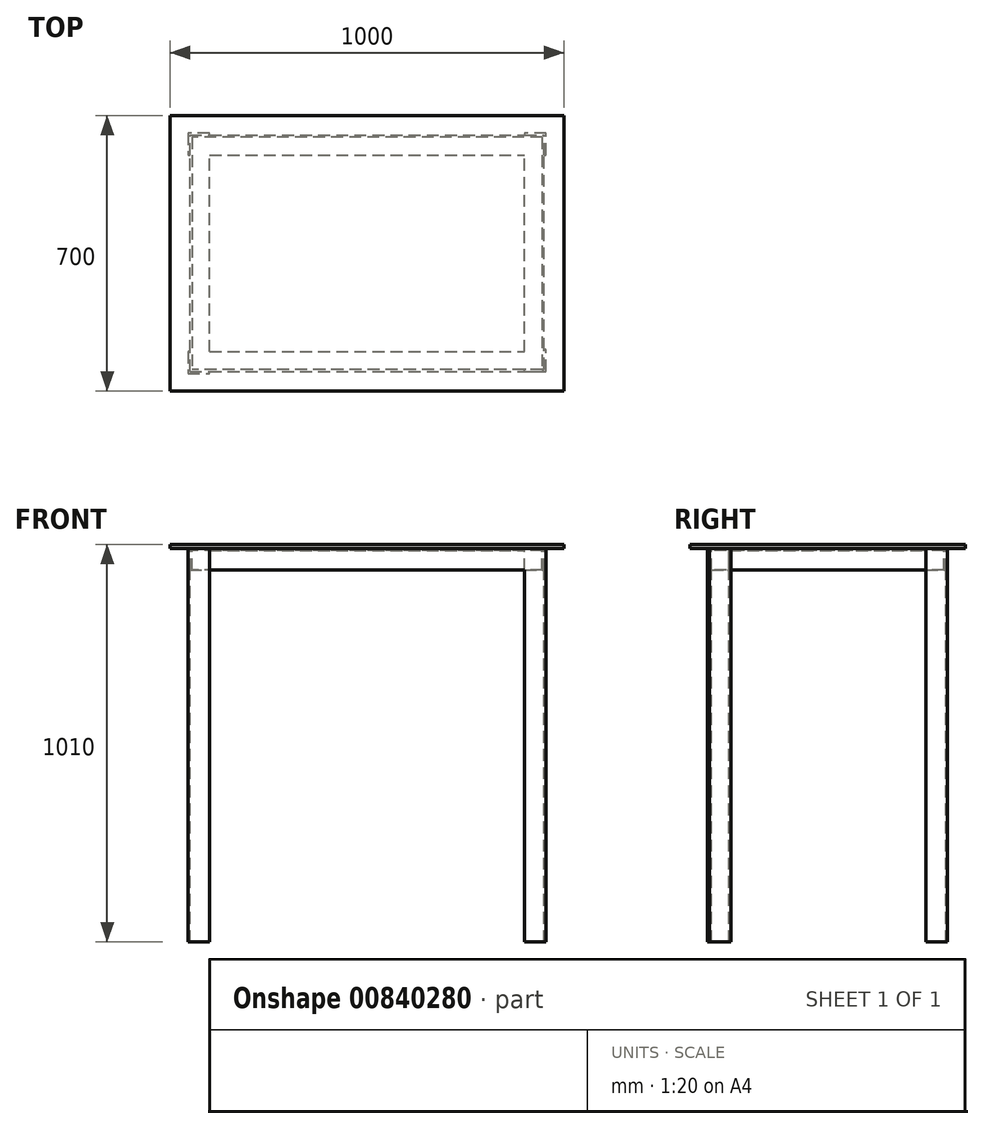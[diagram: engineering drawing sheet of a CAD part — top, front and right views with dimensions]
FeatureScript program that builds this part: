
annotation { "Feature Type Name" : "Feature", "Feature Type Description" : "" }
export const myFeature = defineFeature(function(context is Context, id is Id, definition is map)
    precondition{}
    {
        {
            var Q0;
            Q0=qCreatedBy(makeId("Top.planeOp"),FACE);
            var sketch = newSketch(context, id + "F0", { "sketchPlane" : qUnion([Q0])});
            skLineSegment(sketch, "E0.bottom", {"start": v(-59.03, 659.23) * mm, "end": v(940.97, 659.23) * mm});
            skLineSegment(sketch, "E0.top", {"start": v(-59.03, -40.77) * mm, "end": v(940.97, -40.77) * mm});
            skLineSegment(sketch, "E0.left", {"start": v(-59.03, 659.23) * mm, "end": v(-59.03, -40.77) * mm});
            skLineSegment(sketch, "E0.right", {"start": v(940.97, 659.23) * mm, "end": v(940.97, -40.77) * mm});
            skSolve(sketch);
        }
        {
            var Q0;
            Q0=makeQuery(id+"F0.imprint","IMPRINT",FACE,{"disambiguationData":[TD([[makeQuery(id+"F0.imprint","IMPRINT",EDGE,{"derivedFrom":sQuery(id+"F0.wireOp",EDGE,"E0.bottom")}),-1.0]])]});
            extrude(context, id + "F1", {"entities" : qUnion([Q0]), "oppositeDirection" : true, "depth" : 10 * mm, "offsetDistance" : 25 * mm});
        }
        {
            var Q0;
            Q0=makeQuery(id+"F1.opExtrude","CAP_FACE",FACE,{"disambiguationData":[OSD([sQuery(id+"F0.wireOp",EDGE,"E0.bottom"),sQuery(id+"F0.wireOp",EDGE,"E0.top"),sQuery(id+"F0.wireOp",EDGE,"E0.left"),sQuery(id+"F0.wireOp",EDGE,"E0.right")])],"isStart":false});
            var sketch = newSketch(context, id + "F2", { "sketchPlane" : qUnion([Q0])});
            skLineSegment(sketch, "E1.bottom", {"start": v(-9.03, -9.23) * mm, "end": v(890.97, -9.23) * mm});
            skLineSegment(sketch, "E1.top", {"start": v(-9.03, -609.23) * mm, "end": v(890.97, -609.23) * mm});
            skLineSegment(sketch, "E1.left", {"start": v(-9.03, -9.23) * mm, "end": v(-9.03, -609.23) * mm});
            skLineSegment(sketch, "E1.right", {"start": v(890.97, -9.23) * mm, "end": v(890.97, -609.23) * mm});
            skLineSegment(sketch, "E2.bottom", {"start": v(40.97, -59.23) * mm, "end": v(840.97, -59.23) * mm});
            skLineSegment(sketch, "E2.top", {"start": v(40.97, -559.23) * mm, "end": v(840.97, -559.23) * mm});
            skLineSegment(sketch, "E2.left", {"start": v(40.97, -59.23) * mm, "end": v(40.97, -559.23) * mm});
            skLineSegment(sketch, "E2.right", {"start": v(840.97, -59.23) * mm, "end": v(840.97, -559.23) * mm});
            skSolve(sketch);
        }
        {
            var Q0;
            Q0=makeQuery(id+"F2.imprint","IMPRINT",FACE,{"disambiguationData":[TD([[makeQuery(id+"F2.imprint","IMPRINT",EDGE,{"derivedFrom":sQuery(id+"F2.wireOp",EDGE,"E1.bottom")}),-1.0]])]});
            extrude(context, id + "F3", {"entities" : qUnion([Q0]), "operationType" : NewBodyOperationType.ADD, "oppositeDirection" : true, "depth" : -5 * mm, "offsetDistance" : 25 * mm});
        }
        {
            var Q0;
            Q0=makeQuery(id+"F3.opExtrude","CAP_FACE",FACE,{"disambiguationData":[OSD([sQuery(id+"F2.wireOp",EDGE,"E1.bottom"),sQuery(id+"F2.wireOp",EDGE,"E1.top"),sQuery(id+"F2.wireOp",EDGE,"E1.left"),sQuery(id+"F2.wireOp",EDGE,"E1.right"),sQuery(id+"F2.wireOp",EDGE,"E2.bottom"),sQuery(id+"F2.wireOp",EDGE,"E2.top"),sQuery(id+"F2.wireOp",EDGE,"E2.left"),sQuery(id+"F2.wireOp",EDGE,"E2.right")])],"isStart":false});
            var sketch = newSketch(context, id + "F4", { "sketchPlane" : qUnion([Q0])});
            skLineSegment(sketch, "E3.bottom", {"start": v(-9.03, -9.23) * mm, "end": v(890.97, -9.23) * mm});
            skLineSegment(sketch, "E3.top", {"start": v(-9.03, -609.23) * mm, "end": v(890.97, -609.23) * mm});
            skLineSegment(sketch, "E3.left", {"start": v(-9.03, -9.23) * mm, "end": v(-9.03, -609.23) * mm});
            skLineSegment(sketch, "E3.right", {"start": v(890.97, -9.23) * mm, "end": v(890.97, -609.23) * mm});
            skLineSegment(sketch, "E4.bottom", {"start": v(885.97, -604.23) * mm, "end": v(-4.03, -604.23) * mm});
            skLineSegment(sketch, "E4.top", {"start": v(885.97, -14.23) * mm, "end": v(-4.03, -14.23) * mm});
            skLineSegment(sketch, "E4.left", {"start": v(885.97, -604.23) * mm, "end": v(885.97, -14.23) * mm});
            skLineSegment(sketch, "E4.right", {"start": v(-4.03, -604.23) * mm, "end": v(-4.03, -14.23) * mm});
            skSolve(sketch);
        }
        {
            var Q0;
            Q0 = qSketchRegion(id + "F4", true);
            extrude(context, id + "F5", {"entities" : qUnion([Q0]), "operationType" : NewBodyOperationType.ADD, "depth" : 50 * mm, "offsetDistance" : 25 * mm});
        }
        {
            var Q0;
            {var subQ0=sQuery(id+"F0.wireOp",EDGE,"E0.left");var subQ1=sQuery(id+"F0.wireOp",EDGE,"E0.top");var subQ2=sQuery(id+"F0.wireOp",EDGE,"E0.right");var subQ3=sQuery(id+"F0.wireOp",EDGE,"E0.bottom");Q0=makeQuery(id+"F3.boolean.opBoolean","SPLIT",FACE,{"disambiguationData":[TD([makeQuery(id+"F1.opExtrude","SWEPT_FACE",FACE,{"disambiguationData":[OSD([subQ3])]})])],"derivedFrom":makeQuery(id+"F1.opExtrude","CAP_FACE",FACE,{"disambiguationData":[OSD([subQ3,subQ1,subQ0,subQ2])],"isStart":false})});}
            var sketch = newSketch(context, id + "F6", { "sketchPlane" : qUnion([Q0])});
            skLineSegment(sketch, "E5", {"start": v(-9.03, -9.23) * mm, "end": v(-9.03, -59.23) * mm});
            skLineSegment(sketch, "E6", {"start": v(-9.03, -59.23) * mm, "end": v(-14.03, -59.23) * mm});
            skLineSegment(sketch, "E7", {"start": v(-14.03, -59.23) * mm, "end": v(-14.03, -4.23) * mm});
            skLineSegment(sketch, "E8", {"start": v(-14.03, -4.23) * mm, "end": v(40.97, -4.23) * mm});
            skLineSegment(sketch, "E9", {"start": v(40.97, -4.23) * mm, "end": v(40.97, -9.23) * mm});
            skLineSegment(sketch, "E10", {"start": v(40.97, -9.23) * mm, "end": v(-9.03, -9.23) * mm});
            skLineSegment(sketch, "E11", {"start": v(-9.03, -609.23) * mm, "end": v(40.97, -609.23) * mm});
            skLineSegment(sketch, "E12", {"start": v(40.97, -609.23) * mm, "end": v(40.97, -614.23) * mm});
            skLineSegment(sketch, "E13", {"start": v(40.97, -614.23) * mm, "end": v(-14.03, -614.23) * mm});
            skLineSegment(sketch, "E14", {"start": v(-14.03, -614.23) * mm, "end": v(-14.03, -559.23) * mm});
            skLineSegment(sketch, "E15", {"start": v(-14.03, -559.23) * mm, "end": v(-9.03, -559.23) * mm});
            skLineSegment(sketch, "E16", {"start": v(-9.03, -559.23) * mm, "end": v(-9.03, -609.23) * mm});
            skLineSegment(sketch, "E17", {"start": v(890.97, -14.23) * mm, "end": v(840.97, -14.23) * mm});
            skLineSegment(sketch, "E18", {"start": v(840.97, -14.23) * mm, "end": v(840.97, -9.23) * mm});
            skLineSegment(sketch, "E19", {"start": v(840.97, -9.23) * mm, "end": v(895.97, -9.23) * mm});
            skLineSegment(sketch, "E20", {"start": v(895.97, -9.23) * mm, "end": v(895.97, -64.23) * mm});
            skLineSegment(sketch, "E21", {"start": v(895.97, -64.23) * mm, "end": v(890.97, -64.23) * mm});
            skLineSegment(sketch, "E22", {"start": v(890.97, -64.23) * mm, "end": v(890.97, -14.23) * mm});
            skLineSegment(sketch, "E23", {"start": v(890.97, -609.23) * mm, "end": v(890.97, -559.23) * mm});
            skLineSegment(sketch, "E24", {"start": v(890.97, -559.23) * mm, "end": v(895.97, -559.23) * mm});
            skLineSegment(sketch, "E25", {"start": v(895.97, -559.23) * mm, "end": v(895.97, -614.23) * mm});
            skLineSegment(sketch, "E26", {"start": v(895.97, -614.23) * mm, "end": v(840.97, -614.23) * mm});
            skLineSegment(sketch, "E27", {"start": v(840.97, -614.23) * mm, "end": v(840.97, -609.23) * mm});
            skLineSegment(sketch, "E28", {"start": v(840.97, -609.23) * mm, "end": v(890.97, -609.23) * mm});
            skSolve(sketch);
        }
        {
            var Q0;
            Q0 = qSketchRegion(id + "F6", true);
            extrude(context, id + "F7", {"entities" : qUnion([Q0]), "operationType" : NewBodyOperationType.ADD, "depth" : 1000 * mm, "offsetDistance" : 25 * mm});
        }
    });
